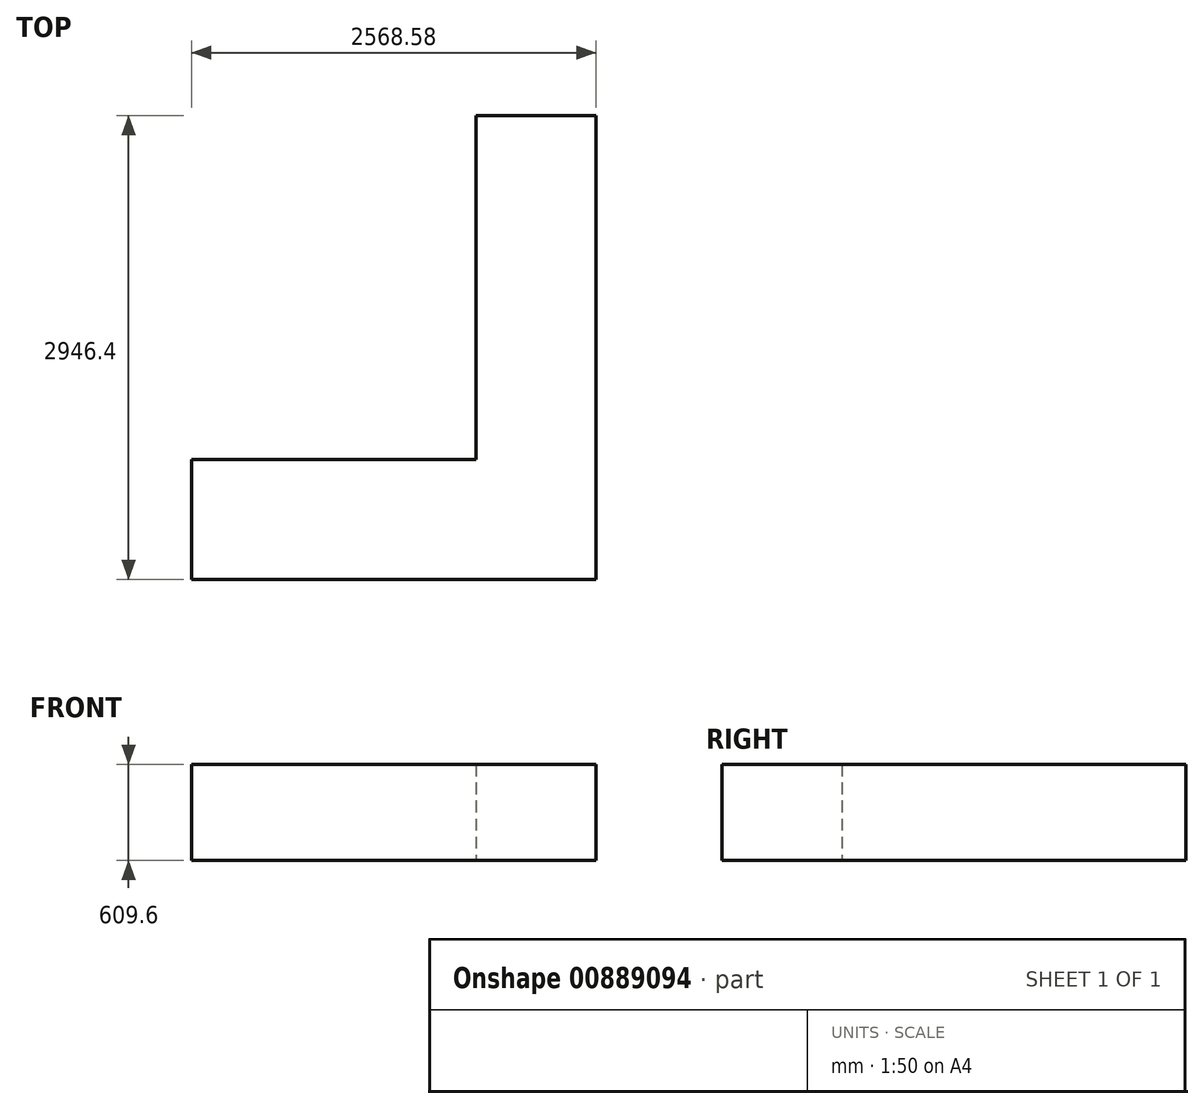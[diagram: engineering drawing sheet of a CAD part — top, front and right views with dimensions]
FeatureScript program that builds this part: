
annotation { "Feature Type Name" : "Feature", "Feature Type Description" : "" }
export const myFeature = defineFeature(function(context is Context, id is Id, definition is map)
    precondition{}
    {
        {
            var Q0;
            Q0=qCreatedBy(makeId("Top.planeOp"),FACE);
            var sketch = newSketch(context, id + "F0", { "sketchPlane" : qUnion([Q0])});
            skLineSegment(sketch, "E0", {"start": v(0, 0) * mm, "end": v(0, -8028.43) * mm});
            skLineSegment(sketch, "E1", {"start": v(0, -8028.43) * mm, "end": v(1289.3, -8028.43) * mm});
            skLineSegment(sketch, "E2", {"start": v(1289.3, -8028.43) * mm, "end": v(1289.3, -8333.23) * mm});
            skLineSegment(sketch, "E3", {"start": v(1289.3, -8333.23) * mm, "end": v(3938.02, -8333.23) * mm});
            skLineSegment(sketch, "E4", {"start": v(3938.02, -8333.23) * mm, "end": v(3938.02, -8028.43) * mm});
            skLineSegment(sketch, "E5", {"start": v(3938.02, -8028.43) * mm, "end": v(7284.72, -8028.43) * mm});
            skLineSegment(sketch, "E6", {"start": v(7284.72, -8028.43) * mm, "end": v(7284.72, -9756.65) * mm});
            skLineSegment(sketch, "E7", {"start": v(7284.72, -9756.65) * mm, "end": v(10927.08, -9756.65) * mm});
            skLineSegment(sketch, "E8", {"start": v(10927.08, -9756.65) * mm, "end": v(10927.08, -9451.85) * mm});
            skLineSegment(sketch, "E9", {"start": v(10927.08, -9451.85) * mm, "end": v(14029.94, -9451.85) * mm});
            skLineSegment(sketch, "E10", {"start": v(14029.94, -9451.85) * mm, "end": v(14029.94, -2816.35) * mm});
            skLineSegment(sketch, "E11", {"start": v(0, 0) * mm, "end": v(3654.55, 0) * mm});
            skLineSegment(sketch, "E12", {"start": v(3654.55, 0) * mm, "end": v(3654.55, 3233.93) * mm});
            skLineSegment(sketch, "E13", {"start": v(3654.55, 3233.93) * mm, "end": v(5349.24, 3233.93) * mm});
            skLineSegment(sketch, "E14", {"start": v(5349.24, 3233.93) * mm, "end": v(5349.24, 3858.77) * mm});
            skLineSegment(sketch, "E15", {"start": v(5349.24, 3858.77) * mm, "end": v(6873.24, 3858.77) * mm});
            skLineSegment(sketch, "E16", {"start": v(6873.24, 3858.77) * mm, "end": v(6873.24, 3233.93) * mm});
            skLineSegment(sketch, "E17", {"start": v(6873.24, 3233.93) * mm, "end": v(8519.16, 3233.93) * mm});
            skLineSegment(sketch, "E18", {"start": v(8519.16, 3233.93) * mm, "end": v(9241.54, 3955.58) * mm});
            skLineSegment(sketch, "E19", {"start": v(9241.54, 3955.58) * mm, "end": v(11405.62, 3955.58) * mm});
            skLineSegment(sketch, "E20", {"start": v(11405.62, 3955.58) * mm, "end": v(12128, 3233.93) * mm});
            skLineSegment(sketch, "E21", {"start": v(12128, 3233.93) * mm, "end": v(14029.94, 3233.93) * mm});
            skLineSegment(sketch, "E22", {"start": v(14029.94, 3233.93) * mm, "end": v(14029.94, 795.53) * mm});
            skLineSegment(sketch, "E23", {"start": v(14029.94, 795.53) * mm, "end": v(14743.5, 82.3) * mm});
            skLineSegment(sketch, "E24", {"start": v(14743.5, 82.3) * mm, "end": v(14743.5, -1752.6) * mm});
            skLineSegment(sketch, "E25", {"start": v(14743.5, -1752.6) * mm, "end": v(14029.94, -2465.83) * mm});
            skLineSegment(sketch, "E26", {"start": v(14029.94, -2465.83) * mm, "end": v(14029.94, -2816.35) * mm});
            skLineSegment(sketch, "E27", {"start": v(14029.94, -2816.35) * mm, "end": v(11719.56, -2816.35) * mm});
            skLineSegment(sketch, "E28", {"start": v(7284.72, -8028.43) * mm, "end": v(7284.72, -3880.1) * mm});
            skLineSegment(sketch, "E29", {"start": v(7284.72, -3880.1) * mm, "end": v(10655.8, -3880.1) * mm});
            skLineSegment(sketch, "E30", {"start": v(10655.8, -3880.1) * mm, "end": v(11719.56, -2816.35) * mm});
            skSolve(sketch);
        }
        {
            var Q0;
            Q0=makeQuery(id+"F0.imprint","IMPRINT",FACE,{"disambiguationData":[TD([[makeQuery(id+"F0.imprint","IMPRINT",EDGE,{"derivedFrom":sQuery(id+"F0.wireOp",EDGE,"E0")}),1.0]])]});
            var sketch = newSketch(context, id + "F1", { "sketchPlane" : qUnion([Q0])});
            skLineSegment(sketch, "E31", {"start": v(5151.12, -8028.43) * mm, "end": v(5151.12, -4539.84) * mm});
            skLineSegment(sketch, "E32", {"start": v(3654.55, 0) * mm, "end": v(3654.55, -1219.2) * mm});
            skLineSegment(sketch, "E33", {"start": v(3654.55, -1219.2) * mm, "end": v(5151.12, -1219.2) * mm});
            skLineSegment(sketch, "E34.bottom", {"start": v(3730.75, 152.4) * mm, "end": v(3578.35, 152.4) * mm});
            skLineSegment(sketch, "E34.top", {"start": v(3730.75, 1066.8) * mm, "end": v(3578.35, 1066.8) * mm});
            skLineSegment(sketch, "E34.left", {"start": v(3730.75, 152.4) * mm, "end": v(3730.75, 1066.8) * mm});
            skLineSegment(sketch, "E34.right", {"start": v(3578.35, 152.4) * mm, "end": v(3578.35, 1066.8) * mm});
            skPoint(sketch, "E34.middle", {"position": v(3654.55, 609.6) * mm});
            skLineSegment(sketch, "E35", {"start": v(7284.72, -3880.1) * mm, "end": v(7284.72, -2660.9) * mm});
            skLineSegment(sketch, "E36", {"start": v(7284.72, -2660.9) * mm, "end": v(6065.52, -2660.9) * mm});
            skLineSegment(sketch, "E37", {"start": v(6065.52, -2660.9) * mm, "end": v(6065.52, -6909.2) * mm});
            skLineSegment(sketch, "E38", {"start": v(6065.52, -6909.2) * mm, "end": v(7286.9, -6909.2) * mm});
            skLineSegment(sketch, "E39", {"start": v(7286.9, -6909.2) * mm, "end": v(7284.72, -3880.1) * mm});
            skLineSegment(sketch, "E40", {"start": v(6065.52, -1219.2) * mm, "end": v(8275.32, -1219.2) * mm});
            skLineSegment(sketch, "E41", {"start": v(8275.32, -1219.2) * mm, "end": v(8275.32, 25.4) * mm});
            skLineSegment(sketch, "E42", {"start": v(8275.32, 25.4) * mm, "end": v(10988.93, 25.4) * mm});
            skLineSegment(sketch, "E43", {"start": v(14029.94, 795.53) * mm, "end": v(12128, 795.53) * mm});
            skLineSegment(sketch, "E44", {"start": v(12128, 795.53) * mm, "end": v(12128, 3233.93) * mm});
            skSolve(sketch);
        }
        {
            var Q0;
            {var subQ3=sQuery(id+"F1.wireOp",EDGE,"E34.left");Q0=makeQuery(id+"F1.imprint","IMPRINT",FACE,{"disambiguationData":[TD([[makeQuery(id+"F1.imprint","IMPRINT",EDGE,{"derivedFrom":subQ3}),-1.0]])]});}
            var sketch = newSketch(context, id + "F2", { "sketchPlane" : qUnion([Q0])});
            skLineSegment(sketch, "E45", {"start": v(8275.32, -1219.2) * mm, "end": v(8275.32, 1727.2) * mm});
            skLineSegment(sketch, "E46", {"start": v(8275.32, 1727.2) * mm, "end": v(7513.32, 1727.2) * mm});
            skLineSegment(sketch, "E47", {"start": v(8275.32, -1219.2) * mm, "end": v(5706.75, -1219.2) * mm});
            skLineSegment(sketch, "E48", {"start": v(5706.75, -1219.2) * mm, "end": v(5706.75, -457.2) * mm});
            skLineSegment(sketch, "E49", {"start": v(5706.75, -457.2) * mm, "end": v(7513.32, -457.2) * mm});
            skLineSegment(sketch, "E50", {"start": v(7513.32, -457.2) * mm, "end": v(7513.32, 1727.2) * mm});
            skSolve(sketch);
        }
        {
            var Q0;
            Q0 = qSketchRegion(id + "F2", true);
            extrude(context, id + "F3", {"entities" : qUnion([Q0]), "depth" : 609.6 * mm, "offsetDistance" : 30.48 * mm});
        }
    });
